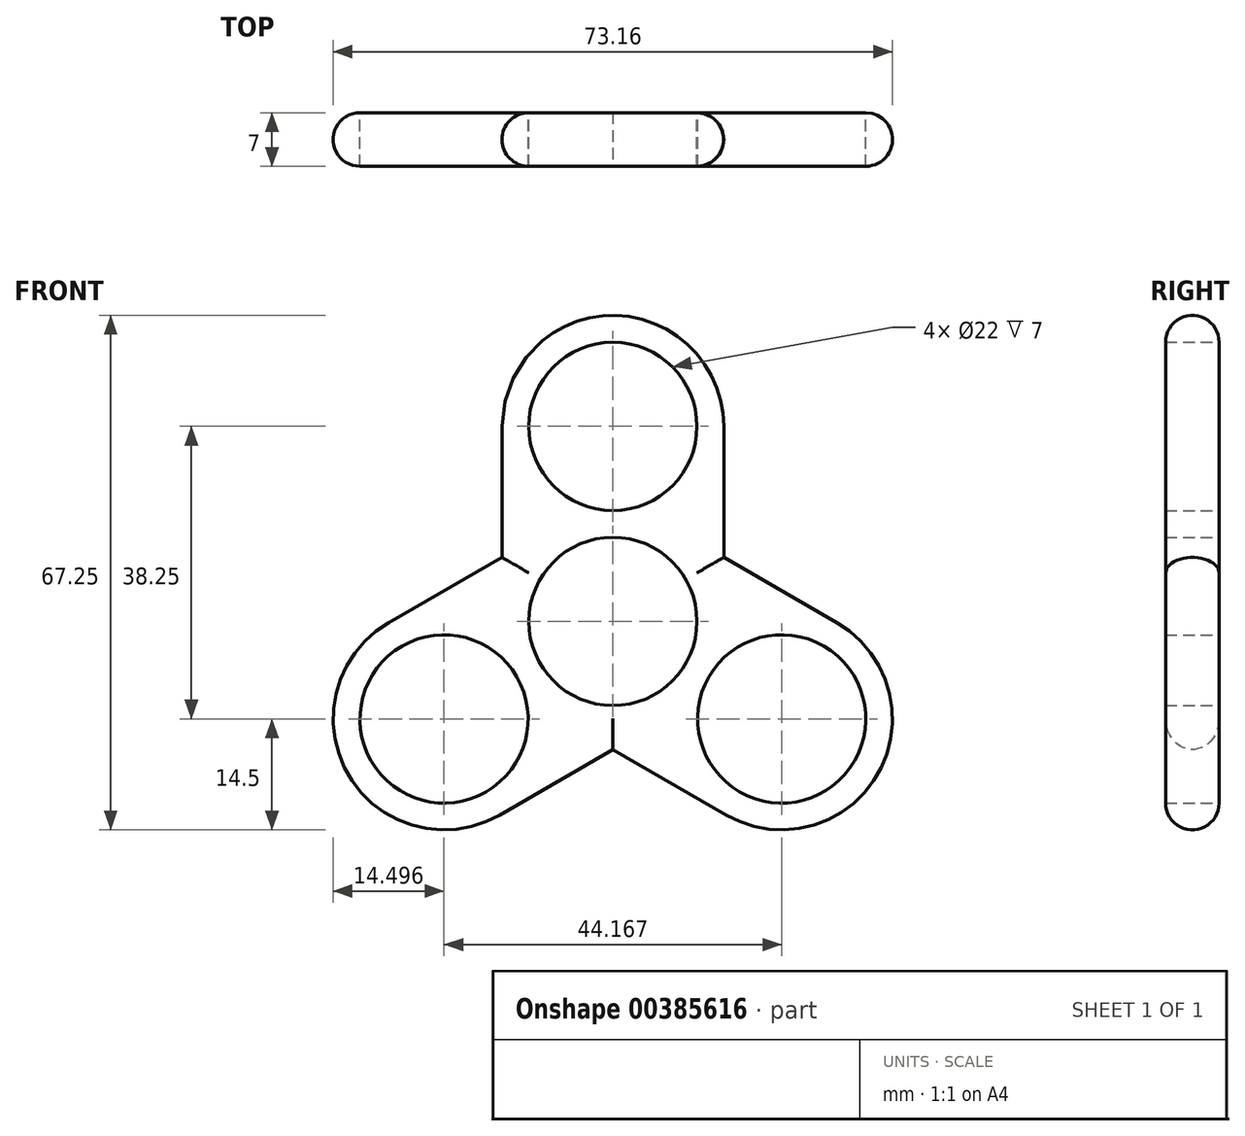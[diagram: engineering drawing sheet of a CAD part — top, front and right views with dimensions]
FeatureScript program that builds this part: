
annotation { "Feature Type Name" : "Feature", "Feature Type Description" : "" }
export const myFeature = defineFeature(function(context is Context, id is Id, definition is map)
    precondition{}
    {
        {
            var Q0;
            Q0=qCreatedBy(makeId("Front.planeOp"),FACE);
            var sketch = newSketch(context, id + "F0", { "sketchPlane" : qUnion([Q0])});
            skCircle(sketch, "E0", {"center": v(0, 0) * mm, "radius": 11 * mm});
            skCircle(sketch, "E1", {"center": v(0, 25.5) * mm, "radius": 11 * mm});
            skArc(sketch, "E2", {"start": v(14.5, 25.5) * mm, "mid": v(0, 40) * mm, "end": v(-14.5, 25.5) * mm});
            skArc(sketch, "E3", {"start": v(-6.9, 12.75) * mm, "mid": v(-7.08, 12.65) * mm, "end": v(-7.25, 12.56) * mm});
            skLineSegment(sketch, "E4", {"start": v(-14.5, 25.5) * mm, "end": v(-14.5, 8.37) * mm});
            skLineSegment(sketch, "E5", {"start": v(14.5, 8.37) * mm, "end": v(14.5, 25.5) * mm});
            skLineSegment(sketch, "E6.1.0", {"start": v(-14.83, -25.3) * mm, "end": v(0, -16.74) * mm});
            skLineSegment(sketch, "E6.1.1", {"start": v(-14.5, 8.37) * mm, "end": v(-29.33, -0.2) * mm});
            skArc(sketch, "E6.1.2", {"start": v(-29.33, -0.2) * mm, "mid": v(-34.64, -20) * mm, "end": v(-14.83, -25.3) * mm});
            skCircle(sketch, "E6.1.3", {"center": v(-22.08, -12.75) * mm, "radius": 11 * mm});
            skLineSegment(sketch, "E6.2.0", {"start": v(29.33, -0.2) * mm, "end": v(14.5, 8.37) * mm});
            skLineSegment(sketch, "E6.2.1", {"start": v(0, -16.74) * mm, "end": v(14.83, -25.3) * mm});
            skArc(sketch, "E6.2.2", {"start": v(14.83, -25.3) * mm, "mid": v(34.64, -20) * mm, "end": v(29.33, -0.2) * mm});
            skCircle(sketch, "E6.2.3", {"center": v(22.08, -12.75) * mm, "radius": 11 * mm});
            skPoint(sketch, "E7.orphan", {"position": v(7.25, 12.56) * mm});
            skPoint(sketch, "E8.orphan", {"position": v(-7.25, 12.56) * mm});
            skArc(sketch, "E9.trimOffspring", {"start": v(-14.5, 0) * mm, "mid": v(-14.5, -0.2) * mm, "end": v(-14.5, -0.4) * mm});
            skArc(sketch, "E10.trimOffspring", {"start": v(7.25, -12.56) * mm, "mid": v(7.42, -12.46) * mm, "end": v(7.59, -12.36) * mm});
            skArc(sketch, "E11.trimOffspring", {"start": v(14.5, -0.4) * mm, "mid": v(14.5, -0.2) * mm, "end": v(14.5, 0) * mm});
            skPoint(sketch, "E12.visualSharp", {"position": v(-14.5, 8.37) * mm});
            skPoint(sketch, "E13.visualSharp", {"position": v(14.5, 8.37) * mm});
            skPoint(sketch, "E14.visualSharp", {"position": v(0, -16.74) * mm});
            skSolve(sketch);
        }
        {
            var Q0;
            Q0=makeQuery(id+"F0.imprint","IMPRINT",FACE,{"disambiguationData":[TD([[makeQuery(id+"F0.imprint","IMPRINT",EDGE,{"derivedFrom":sQuery(id+"F0.wireOp",EDGE,"E0")}),-1.0]])]});
            extrude(context, id + "F1", {"entities" : qUnion([Q0]), "depth" : 7 * mm, "offsetDistance" : 25 * mm});
        }
        {
            var Q0;
            Q0=makeQuery(id+"F1.opExtrude","CAP_EDGE",EDGE,{"disambiguationData":[OSD([sQuery(id+"F0.wireOp",EDGE,"E6.1.1")])],"isStart":false});
            var Q1;
            Q1=makeQuery(id+"F1.opExtrude","CAP_EDGE",EDGE,{"disambiguationData":[OSD([sQuery(id+"F0.wireOp",EDGE,"E5")])],"isStart":false});
            var Q2;
            Q2=makeQuery(id+"F1.opExtrude","CAP_EDGE",EDGE,{"disambiguationData":[OSD([sQuery(id+"F0.wireOp",EDGE,"E6.2.1")])],"isStart":false});
            var Q3;
            Q3=makeQuery(id+"F1.opExtrude","CAP_EDGE",EDGE,{"disambiguationData":[OSD([sQuery(id+"F0.wireOp",EDGE,"E6.2.0")])],"isStart":true});
            var Q4;
            Q4=makeQuery(id+"F1.opExtrude","CAP_EDGE",EDGE,{"disambiguationData":[OSD([sQuery(id+"F0.wireOp",EDGE,"E4")])],"isStart":true});
            var Q5;
            Q5=makeQuery(id+"F1.opExtrude","CAP_EDGE",EDGE,{"disambiguationData":[OSD([sQuery(id+"F0.wireOp",EDGE,"E6.1.0")])],"isStart":true});
            fillet(context, id + "F2", {"entities" : qUnion([Q0, Q1, Q2, Q3, Q4, Q5]), "radius" : 3.5 * mm, "tangentPropagation" : true, "allowEdgeOverflow" : false});
        }
    });
